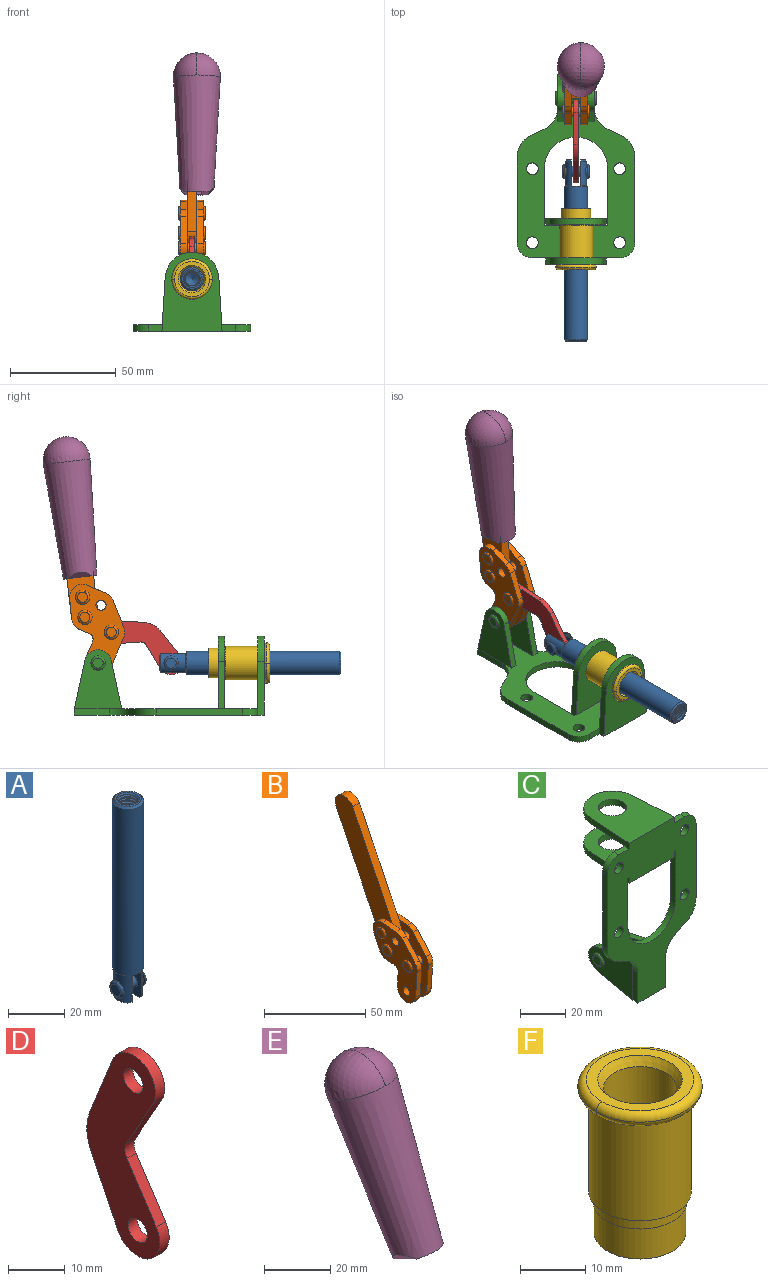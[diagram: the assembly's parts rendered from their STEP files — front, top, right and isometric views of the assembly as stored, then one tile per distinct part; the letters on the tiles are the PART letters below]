
ASSEMBLY  parts=6 mates=6
PART A: 48 faces, bbox 12.6x11.1x86.1 mm
  f0: torus R=2.41mm, axis (-1,0,0), area 15mm2, adj f30,f32,f34
  f1: torus R=2.41mm, axis (-1,0,0), area 15mm2, adj f29,f31,f33
  f2: cylinder r=5.54mm len=72.39mm, axis (0,0,1), area 2518.5mm2, adj f3,f4,f42,f43
  f3: cone r=5.54mm half-angle=45deg, axis (0,0,1), area 7.6mm2, adj f2,f5,f41
  f4: cone r=5.54mm half-angle=45deg, axis (0,0,-1), area 34.9mm2, adj f2,f39
  f5: cylinder r=5.08mm len=11.48mm, axis (0,0,1), area 108.3mm2, adj f3,f7,f8,f41
  f6: cylinder r=2.41mm len=4.83mm, axis (-1,0,0), area 71.2mm2, adj f40,f41
  f7: cylinder r=2.41mm len=4.83mm, axis (-1,0,0), area 7.6mm2, adj f5,f34
  f8: cone r=5.08mm half-angle=45deg, axis (0,0,1), area 10.6mm2, adj f5,f37,f41
  f9: cone r=3.98mm half-angle=45deg, axis (0,0,1), area 17.6mm2, adj f27,f39,f45,f46,f47
  f10: cylinder r=2.41mm len=4.83mm, axis (-1,0,0), area 7.6mm2, adj f33,f38
  f11: cylinder r=3.2mm len=6.4mm, axis (0,0,1), area 78.4mm2, adj f12,f28,f44,f45,f47
  f12: cylinder r=3.2mm len=6.4mm, axis (0,0,1), area 10.5mm2, adj f11,f13,f45,f47
  f13: cylinder r=3.2mm len=6.4mm, axis (0,0,1), area 10.5mm2, adj f12,f14,f45,f47
  f14: cylinder r=3.2mm len=6.4mm, axis (0,0,1), area 10.5mm2, adj f13,f15,f45,f47
  f15: cylinder r=3.2mm len=6.4mm, axis (0,0,1), area 10.5mm2, adj f14,f16,f45,f47
  f16: cylinder r=3.2mm len=6.4mm, axis (0,0,1), area 10.5mm2, adj f15,f17,f45,f47
  f17: cylinder r=3.2mm len=6.4mm, axis (0,0,1), area 10.5mm2, adj f16,f18,f45,f47
  f18: cylinder r=3.2mm len=6.4mm, axis (0,0,1), area 10.5mm2, adj f17,f19,f45,f47
  f19: cylinder r=3.2mm len=6.4mm, axis (0,0,1), area 10.5mm2, adj f18,f20,f45,f47
  f20: cylinder r=3.2mm len=6.4mm, axis (0,0,1), area 10.5mm2, adj f19,f21,f45,f47
  f21: cylinder r=3.2mm len=6.4mm, axis (0,0,1), area 10.5mm2, adj f20,f22,f45,f47
  f22: cylinder r=3.2mm len=6.4mm, axis (0,0,1), area 10.5mm2, adj f21,f23,f45,f47
  f23: cylinder r=3.2mm len=6.4mm, axis (0,0,1), area 10.5mm2, adj f22,f24,f45,f47
  f24: cylinder r=3.2mm len=6.4mm, axis (0,0,1), area 10.5mm2, adj f23,f25,f45,f47
  f25: cylinder r=3.2mm len=6.4mm, axis (0,0,1), area 10.5mm2, adj f24,f26,f45,f47
  f26: cylinder r=3.2mm len=6.4mm, axis (0,0,1), area 10.5mm2, adj f25,f27,f45,f47
  f27: cylinder r=3.2mm len=6.4mm, axis (0,0,1), area 7.4mm2, adj f9,f26,f45,f47
  f28: cone r=3.2mm half-angle=60deg, axis (0,0,1), area 37.2mm2, adj f11
  f29: plane 4.83x4.83mm, normal (-1,0,0), area 18.3mm2, adj f1,f31
  f30: plane 4.83x4.83mm, normal (1,0,0), area 18.3mm2, adj f0,f32
  f31: torus R=2.41mm, axis (-1,0,0), area 15mm2, adj f1,f29,f33
  f32: torus R=2.41mm, axis (-1,0,0), area 15mm2, adj f0,f30,f34
  f33: plane 6.83x6.83mm, normal (1,0,0), area 18.3mm2, adj f1,f10,f31
  f34: plane 6.83x6.83mm, normal (-1,0,0), area 18.3mm2, adj f0,f7,f32
  f35: cone r=5.08mm half-angle=45deg, axis (0,0,1), area 10.6mm2, adj f36,f38,f40
  f36: plane 7.25x1.97mm, normal (0,0,-1), area 10mm2, adj f35,f40
  f37: plane 7.25x1.97mm, normal (0,0,-1), area 10mm2, adj f8,f41
  f38: cylinder r=5.08mm len=11.48mm, axis (0,0,1), area 108.3mm2, adj f10,f35,f40,f42
  f39: plane 9.55x9.55mm, normal (0,0,1), area 22mm2, adj f4,f9
  f40: plane 12.76x10.09mm, normal (1,0,0), area 95.7mm2, adj f6,f35,f36,f38,f42,f43
  f41: plane 12.76x10.09mm, normal (-1,0,0), area 95.7mm2, adj f3,f5,f6,f8,f37,f43
  f42: cone r=5.54mm half-angle=45deg, axis (0,0,1), area 7.6mm2, adj f2,f38,f40
  f43: plane 11.07x4.7mm, normal (0,0,-1), area 50.4mm2, adj f2,f40,f41
  f44: plane 0.89x0.62mm, normal (-1,0,0), area 0.3mm2, adj f11,f45,f46,f47
  f45: bspline ~24.8x7.63mm, area 266.6mm2, adj f9,f11,f12,f13,f14,f15,f16,f17
  f46: bspline ~24.87x7.63mm, area 73.6mm2, adj f9,f44,f45,f47
  f47: bspline ~24.98x7.63mm, area 272.5mm2, adj f9,f11,f12,f13,f14,f15,f16,f17
PART B: 59 faces, bbox 12.9x60.2x99.6 mm
  f0: torus R=2.39mm, axis (-1,0,0), area 14.9mm2, adj f20,f43,f51
  f1: torus R=2.39mm, axis (-1,0,0), area 14.9mm2, adj f19,f42,f51
  f2: torus R=2.39mm, axis (-1,0,0), area 14.9mm2, adj f18,f35,f51
  f3: torus R=2.39mm, axis (-1,0,0), area 14.9mm2, adj f14,f17,f23
  f4: torus R=2.39mm, axis (-1,0,0), area 14.9mm2, adj f13,f16,f23
  f5: torus R=2.39mm, axis (-1,0,0), area 14.9mm2, adj f12,f15,f23
  f6: cylinder r=2.39mm len=4.78mm, axis (1,0,0), area 46.5mm2, adj f48,f50,f51
  f7: cylinder r=2.39mm len=4.78mm, axis (1,0,0), area 46.5mm2, adj f50,f51
  f8: cylinder r=6.35mm len=12.68mm, axis (1,0,0), area 61.8mm2, adj f38,f39,f50,f51
  f9: cylinder r=2.39mm len=4.78mm, axis (-1,0,0), area 70.5mm2, adj f46,f50
  f10: cylinder r=2.39mm len=4.78mm, axis (-1,0,0), area 46.5mm2, adj f23,f45,f46
  f11: cylinder r=2.39mm len=4.78mm, axis (-1,0,0), area 46.5mm2, adj f23,f46
  f12: plane 4.78x4.78mm, normal (1,0,0), area 17.9mm2, adj f5,f15
  f13: plane 4.78x4.78mm, normal (1,0,0), area 17.9mm2, adj f4,f16
  f14: plane 4.78x4.78mm, normal (1,0,0), area 17.9mm2, adj f3,f17
  f15: torus R=2.39mm, axis (-1,0,0), area 14.9mm2, adj f5,f12,f23
  f16: torus R=2.39mm, axis (-1,0,0), area 14.9mm2, adj f4,f13,f23
  f17: torus R=2.39mm, axis (-1,0,0), area 14.9mm2, adj f3,f14,f23
  f18: plane 4.78x4.78mm, normal (-1,0,0), area 17.9mm2, adj f2,f35
  f19: plane 4.78x4.78mm, normal (-1,0,0), area 17.9mm2, adj f1,f42
  f20: plane 4.78x4.78mm, normal (-1,0,0), area 17.9mm2, adj f0,f43
  f21: plane 2.26x0.2mm, normal (1,0,0), area 0.2mm2, adj f31,f44
  f22: plane 2.26x0.2mm, normal (-1,0,0), area 0.2mm2, adj f41,f44
  f23: plane 39.37x30.77mm, normal (1,0,0), area 565.5mm2, adj f3,f4,f5,f10,f11,f15,f16,f17
  f24: cylinder r=6.1mm len=4.15mm, axis (-1,0,0), area 14.7mm2, adj f23,f25,f32,f46
  f25: plane 10.25x9.01mm, normal (0,-0.75,0.66), area 42.3mm2, adj f23,f24,f26,f46
  f26: cylinder r=6.35mm len=4.64mm, axis (-1,0,0), area 15.6mm2, adj f23,f25,f27,f46
  f27: plane 15.84x3.1mm, normal (0,-1,-0.07), area 49.2mm2, adj f23,f26,f28,f46
  f28: cylinder r=6.35mm len=12.68mm, axis (-1,0,0), area 61.8mm2, adj f23,f27,f29,f46
  f29: plane 8.11x3.1mm, normal (0,1,0.07), area 25.2mm2, adj f23,f28,f30,f46
  f30: cylinder r=3.05mm len=3.25mm, axis (-1,0,0), area 14.8mm2, adj f23,f29,f31,f46
  f31: plane 5.99x3.1mm, normal (0,0.07,-1), area 18.6mm2, adj f21,f23,f30,f44,f46
  f32: plane 9.5x3.1mm, normal (0,-0.07,1), area 29.5mm2, adj f23,f24,f33,f46,f47
  f33: cylinder r=6.1mm len=8.63mm, axis (-1,0,0), area 39.1mm2, adj f23,f32,f34,f47
  f34: plane 8.65x3.96mm, normal (0,0.91,-0.42), area 29.5mm2, adj f23,f33,f44,f47
  f35: torus R=2.39mm, axis (-1,0,0), area 14.9mm2, adj f2,f18,f51
  f36: plane 10.25x9.01mm, normal (0,-0.75,0.66), area 42.3mm2, adj f37,f49,f50,f51
  f37: cylinder r=6.35mm len=4.64mm, axis (1,0,0), area 15.6mm2, adj f36,f38,f50,f51
  f38: plane 15.84x3.1mm, normal (0,-1,-0.07), area 49.2mm2, adj f8,f37,f50,f51
  f39: plane 8.11x3.1mm, normal (0,1,0.07), area 25.2mm2, adj f8,f40,f50,f51
  f40: cylinder r=3.05mm len=3.25mm, axis (1,0,0), area 14.8mm2, adj f39,f41,f50,f51
  f41: plane 5.99x3.1mm, normal (0,0.07,-1), area 18.6mm2, adj f22,f40,f44,f50,f51
  f42: torus R=2.39mm, axis (-1,0,0), area 14.9mm2, adj f1,f19,f51
  f43: torus R=2.39mm, axis (-1,0,0), area 14.9mm2, adj f0,f20,f51
  f44: cylinder r=6.35mm len=12.12mm, axis (-1,0,0), area 128.9mm2, adj f21,f22,f23,f31,f34,f41,f46,f47
  f45: plane 2.65x1.35mm, normal (1,0,0), area 1mm2, adj f10,f55
  f46: plane 39.08x20.42mm, normal (-1,0,0), area 412.5mm2, adj f9,f10,f11,f24,f25,f26,f27,f28
  f47: plane 77.62x39.82mm, normal (1,0,0), area 850mm2, adj f32,f33,f34,f44,f53,f54,f55
  f48: plane 2.65x1.35mm, normal (-1,0,0), area 1mm2, adj f6,f55
  f49: cylinder r=6.1mm len=4.15mm, axis (1,0,0), area 14.7mm2, adj f36,f50,f51,f56
  f50: plane 39.08x20.42mm, normal (1,0,0), area 412.5mm2, adj f6,f7,f8,f9,f36,f37,f38,f39
  f51: plane 39.37x30.77mm, normal (-1,0,0), area 565.5mm2, adj f0,f1,f2,f6,f7,f8,f35,f36
  f52: plane 8.65x3.96mm, normal (0,0.91,-0.42), area 29.5mm2, adj f44,f51,f57,f58
  f53: plane 68.49x33.4mm, normal (0,0.9,-0.44), area 358.1mm2, adj f44,f47,f54,f58
  f54: cylinder r=6.35mm len=12.06mm, axis (1,0,0), area 93.7mm2, adj f47,f53,f55,f58
  f55: plane 68.49x33.4mm, normal (0,-0.9,0.44), area 358.1mm2, adj f44,f45,f46,f47,f48,f50,f54,f58
  f56: plane 9.5x3.1mm, normal (0,-0.07,1), area 29.5mm2, adj f49,f50,f51,f57,f58
  f57: cylinder r=6.1mm len=8.63mm, axis (1,0,0), area 39.1mm2, adj f51,f52,f56,f58
  f58: plane 77.62x39.82mm, normal (-1,0,0), area 850mm2, adj f44,f52,f53,f54,f55,f56,f57
PART C: 55 faces, bbox 55.7x37.4x89.8 mm
  f0: torus R=2.41mm, axis (-1,0,0), area 15mm2, adj f11,f15,f25
  f1: torus R=2.41mm, axis (-1,0,0), area 15mm2, adj f10,f12,f22
  f2: cylinder r=2.78mm len=5.56mm, axis (0,-1,0), area 54.2mm2, adj f30,f54
  f3: cylinder r=14.99mm len=29.97mm, axis (0,-1,0), area 145.9mm2, adj f30,f49,f53,f54
  f4: cylinder r=2.78mm len=5.56mm, axis (0,-1,0), area 54.2mm2, adj f30,f54
  f5: cylinder r=2.78mm len=5.56mm, axis (0,-1,0), area 54.2mm2, adj f30,f54
  f6: cylinder r=2.78mm len=5.56mm, axis (0,-1,0), area 54.2mm2, adj f30,f54
  f7: cylinder r=6.35mm len=12.7mm, axis (0,0,1), area 123.6mm2, adj f27,f51
  f8: cylinder r=6.35mm len=12.7mm, axis (0,0,-1), area 124.7mm2, adj f21,f35
  f9: cylinder r=2.41mm len=11.18mm, axis (-1,0,0), area 169.4mm2, adj f16,f19
  f10: plane 4.83x4.83mm, normal (1,0,0), area 18.3mm2, adj f1,f12
  f11: plane 4.83x4.83mm, normal (-1,0,0), area 18.3mm2, adj f0,f15
  f12: torus R=2.41mm, axis (-1,0,0), area 15mm2, adj f1,f10,f22
  f13: cylinder r=6.35mm len=12.41mm, axis (1,0,0), area 53.4mm2, adj f18,f19,f22,f23
  f14: cylinder r=6.35mm len=12.41mm, axis (-1,0,0), area 53.4mm2, adj f16,f17,f24,f25
  f15: torus R=2.41mm, axis (-1,0,0), area 15mm2, adj f0,f11,f25
  f16: plane 27.86x22.35mm, normal (1,0,0), area 425.4mm2, adj f9,f14,f17,f24,f30
  f17: plane 22.86x4.97mm, normal (0,0.21,0.98), area 72.5mm2, adj f14,f16,f25,f30
  f18: plane 22.86x4.97mm, normal (0,0.21,0.98), area 72.5mm2, adj f13,f19,f22,f30
  f19: plane 27.86x22.35mm, normal (-1,0,0), area 425.4mm2, adj f9,f13,f18,f23,f30
  f20: cylinder r=12.7mm len=25.35mm, axis (0,0,-1), area 119.8mm2, adj f21,f34,f35,f36
  f21: plane 34.21x28.07mm, normal (0,0,-1), area 702.4mm2, adj f8,f20,f30,f34,f36
  f22: plane 27.96x22.45mm, normal (1,0,0), area 407.2mm2, adj f1,f12,f13,f18,f23,f30,f42,f43
  f23: plane 22.86x4.97mm, normal (0,0.21,-0.98), area 72.5mm2, adj f13,f19,f22,f44
  f24: plane 22.86x4.97mm, normal (0,0.21,-0.98), area 72.5mm2, adj f14,f16,f25,f44
  f25: plane 27.86x22.35mm, normal (-1,0,0), area 407.1mm2, adj f0,f14,f15,f17,f24,f30,f45,f46
  f26: plane 3.1x0.95mm, normal (0,0,-1), area 2.7mm2, adj f30,f49,f50,f54
  f27: plane 34.21x28.07mm, normal (0,0,1), area 702.4mm2, adj f7,f28,f30,f50,f52
  f28: cylinder r=12.7mm len=25.35mm, axis (0,0,1), area 118.8mm2, adj f27,f50,f51,f52
  f29: plane 3.1x0.95mm, normal (0,0,-1), area 2.7mm2, adj f30,f52,f53,f54
  f30: plane 86.54x55.63mm, normal (0,1,0), area 2362.9mm2, adj f2,f3,f4,f5,f6,f16,f17,f18
  f31: plane 40.56x3.1mm, normal (-1,0,0), area 125.7mm2, adj f30,f32,f48,f54
  f32: cylinder r=7.11mm len=7.11mm, axis (0,-1,0), area 34.6mm2, adj f30,f31,f33,f54
  f33: plane 6.67x3.1mm, normal (0,0,1), area 20.4mm2, adj f30,f32,f34,f54
  f34: plane 25.39x3.13mm, normal (-1,0.06,0), area 79.5mm2, adj f20,f21,f33,f35,f54
  f35: plane 37.31x28.45mm, normal (0,0,1), area 789.9mm2, adj f8,f20,f34,f36,f54
  f36: plane 25.39x3.13mm, normal (1,0.06,0), area 79.5mm2, adj f20,f21,f35,f37,f54
  f37: plane 6.67x3.1mm, normal (0,0,1), area 20.4mm2, adj f30,f36,f38,f54
  f38: cylinder r=7.11mm len=7.11mm, axis (0,-1,0), area 34.6mm2, adj f30,f37,f39,f54
  f39: plane 40.56x3.1mm, normal (1,0,0), area 125.7mm2, adj f30,f38,f40,f54
  f40: cylinder r=11.18mm len=10.16mm, axis (0,-1,0), area 39.5mm2, adj f30,f39,f41,f54
  f41: plane 6.09x3.1mm, normal (0.42,0,-0.91), area 20.8mm2, adj f30,f40,f42,f54
  f42: cylinder r=11.18mm len=9.41mm, axis (0,-1,0), area 37.2mm2, adj f22,f30,f41,f43,f54
  f43: plane 16.5x3.1mm, normal (1,0,0), area 51.1mm2, adj f22,f42,f44,f54
  f44: plane 17.37x3.1mm, normal (0,0,-1), area 53.8mm2, adj f23,f24,f30,f43,f45,f54
  f45: plane 16.5x3.1mm, normal (-1,0,0), area 51.1mm2, adj f25,f44,f46,f54
  f46: cylinder r=11.18mm len=9.41mm, axis (0,-1,0), area 37.2mm2, adj f25,f30,f45,f47,f54
  f47: plane 6.09x3.1mm, normal (-0.42,0,-0.91), area 20.8mm2, adj f30,f46,f48,f54
  f48: cylinder r=11.18mm len=10.16mm, axis (0,-1,0), area 39.5mm2, adj f30,f31,f47,f54
  f49: plane 26.54x3.1mm, normal (-1,0,0), area 82.3mm2, adj f3,f26,f30,f54
  f50: plane 25.39x3.1mm, normal (1,0.06,0), area 78.8mm2, adj f26,f27,f28,f51,f54
  f51: plane 37.31x28.45mm, normal (0,0,-1), area 789.9mm2, adj f7,f28,f50,f52,f54
  f52: plane 25.39x3.1mm, normal (-1,0.06,0), area 78.8mm2, adj f27,f28,f29,f51,f54
  f53: plane 26.54x3.1mm, normal (1,0,0), area 82.3mm2, adj f3,f29,f30,f54
  f54: plane 89.66x55.63mm, normal (0,-1,0), area 2678.5mm2, adj f2,f3,f4,f5,f6,f26,f29,f31
PART D: 12 faces, bbox 2.3x18.2x42.8 mm
  f0: cylinder r=2.4mm len=4.8mm, axis (1,0,0), area 34.9mm2, adj f4,f11
  f1: cylinder r=10.41mm len=8.47mm, axis (1,0,0), area 20.2mm2, adj f4,f9,f10,f11
  f2: cylinder r=3.05mm len=3.16mm, axis (1,0,0), area 7.7mm2, adj f4,f6,f7,f11
  f3: cylinder r=2.4mm len=4.8mm, axis (1,0,0), area 34.9mm2, adj f4,f11
  f4: plane 42.81x18.23mm, normal (-1,0,0), area 414.1mm2, adj f0,f1,f2,f3,f5,f6,f7,f8
  f5: cylinder r=5.54mm len=10.67mm, axis (1,0,0), area 41.8mm2, adj f4,f6,f10,f11
  f6: plane 11.66x6.53mm, normal (0,-0.87,-0.49), area 30.9mm2, adj f2,f4,f5,f11
  f7: plane 11.17x7.33mm, normal (0,-0.84,0.55), area 30.9mm2, adj f2,f4,f8,f11
  f8: cylinder r=5.54mm len=10.51mm, axis (1,0,0), area 41.8mm2, adj f4,f7,f9,f11
  f9: plane 13.67x6.67mm, normal (0,0.9,-0.44), area 35.1mm2, adj f1,f4,f8,f11
  f10: plane 14.1x5.7mm, normal (0,0.93,0.37), area 35.1mm2, adj f1,f4,f5,f11
  f11: plane 42.81x18.23mm, normal (1,0,0), area 414.1mm2, adj f0,f1,f2,f3,f5,f6,f7,f8
PART E: 11 faces, bbox 22.3x42.6x64.5 mm
  f0: sphere r=11.13mm, area 411.4mm2, adj f1,f8
  f1: cone r=11.11mm half-angle=3.3deg, axis (0,0.44,0.9), area 3251.8mm2, adj f0,f7,f8,f9,f10
  f2: cylinder r=6.16mm len=11.7mm, axis (1,0,0), area 89.5mm2, adj f3,f4,f5,f6
  f3: plane 60.23x36.75mm, normal (-1,0,0), area 763.6mm2, adj f2,f4,f6,f10
  f4: plane 51.37x25.05mm, normal (0,0.9,-0.44), area 264.2mm2, adj f2,f3,f5,f10
  f5: plane 60.23x36.75mm, normal (1,0,0), area 763.6mm2, adj f2,f4,f6,f10
  f6: plane 51.37x25.05mm, normal (0,-0.9,0.44), area 264.2mm2, adj f2,f3,f5,f10
  f7: plane 9.95x5.95mm, normal (0.71,-0.31,-0.64), area 25.8mm2, adj f1,f10
  f8: sphere r=11.13mm, area 411.4mm2, adj f0,f1
  f9: plane 9.95x5.95mm, normal (-0.71,-0.31,-0.64), area 25.8mm2, adj f1,f10
  f10: plane 14.27x11.38mm, normal (0,-0.44,-0.9), area 106.7mm2, adj f1,f3,f4,f5,f6,f7,f9
PART F: 15 faces, bbox 20.6x20.6x28.7 mm
  f0: torus R=8.26mm, axis (0,0,1), area 56.8mm2, adj f1,f10,f12
  f1: torus R=8.26mm, axis (0,0,1), area 56.8mm2, adj f0,f6,f13
  f2: cylinder r=5.59mm len=25.91mm, axis (0,0,1), area 909.6mm2, adj f3,f4
  f3: cone r=6.86mm half-angle=45deg, axis (0,0,-1), area 70.2mm2, adj f2,f14
  f4: cone r=6.47mm half-angle=30deg, axis (0,0,1), area 66.7mm2, adj f2,f13
  f5: cylinder r=7.04mm len=14.07mm, axis (0,0,1), area 252.6mm2, adj f11,f14
  f6: torus R=8.26mm, axis (0,0,1), area 56.8mm2, adj f1,f12,f13
  f7: cylinder r=7.16mm len=14.33mm, axis (0,0,1), area 91.5mm2, adj f9,f11
  f8: cylinder r=7.86mm len=18.42mm, axis (0,0,1), area 909.6mm2, adj f9,f10
  f9: plane 15.72x15.72mm, normal (0,0,-1), area 33mm2, adj f7,f8
  f10: plane 16.51x16.51mm, normal (0,0,-1), area 19.9mm2, adj f0,f8,f12
  f11: plane 14.33x14.33mm, normal (0,0,-1), area 5.7mm2, adj f5,f7
  f12: torus R=8.26mm, axis (0,0,1), area 56.8mm2, adj f0,f6,f10
  f13: plane 16.51x16.51mm, normal (0,0,1), area 82.7mm2, adj f1,f4,f6
  f14: plane 14.07x14.07mm, normal (0,0,-1), area 7.8mm2, adj f3,f5
PLACE A rot(axis=(1,0,0),90deg) t=(0,22.21,0)mm
PLACE B rot(axis=(1,0,0),19.3deg) t=(0,7.39,46.75)mm
PLACE C rot(axis=(1,0,0),90deg) t=(0,9.14,0)mm fixed
PLACE D rot(axis=(1,0,0),119.3deg) t=(0,32.29,10.73)mm
PLACE E rot(axis=(1,0,0),19.3deg) t=(2.31,7.39,46.75)mm
PLACE F rot(axis=(1,0,0),90deg) t=(0,9.14,0)mm
MATE revolute B.f7 <-> C.f0  axis (1,0,0) through (0,41.23,24.61)mm
MATE fastened F.f2 <-> C.f7  axis (0,-1,0) through (0,-37.25,24.61)mm
MATE fastened E.f2 <-> B.f54  axis (1,0,0) through (0,56.29,121.95)mm
MATE slider A.f2 <-> C.f7  axis (0,-1,0) through (0,-36.57,24.61)mm
MATE revolute D.f3 <-> B.f4  axis (1,0,0) through (0,34.95,39.19)mm
MATE revolute D.f5 <-> A.f6  axis (1,0,0) through (0,6.74,24.61)mm
